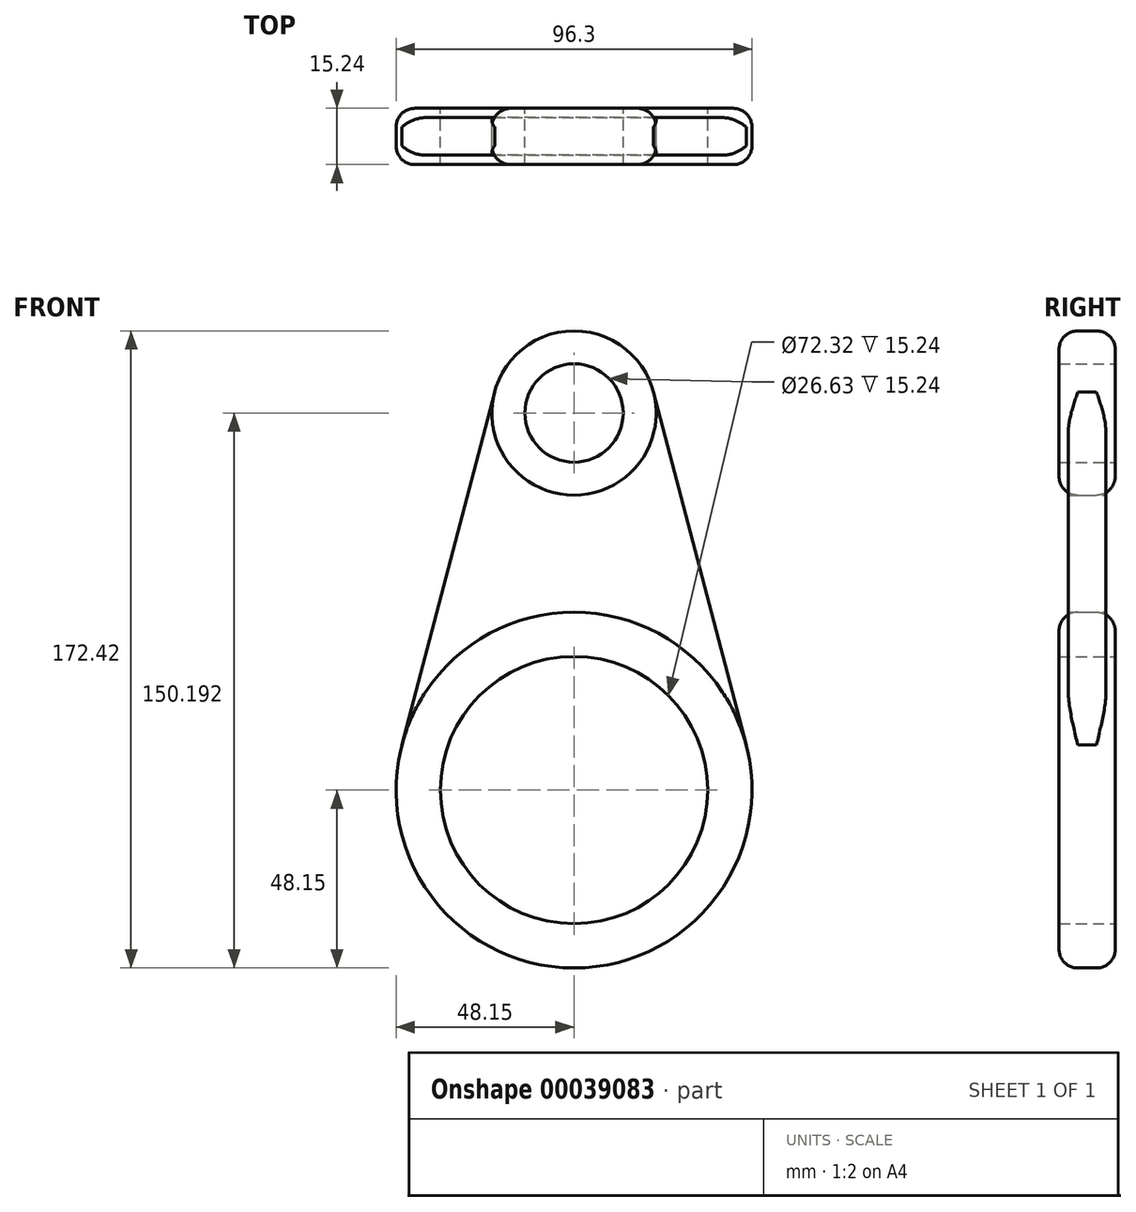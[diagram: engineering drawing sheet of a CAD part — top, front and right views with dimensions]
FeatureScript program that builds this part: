
annotation { "Feature Type Name" : "Feature", "Feature Type Description" : "" }
export const myFeature = defineFeature(function(context is Context, id is Id, definition is map)
    precondition{}
    {
        {
            var Q0;
            Q0=qCreatedBy(makeId("Front.planeOp"),FACE);
            var sketch = newSketch(context, id + "F0", { "sketchPlane" : qUnion([Q0])});
            skCircle(sketch, "E0", {"center": v(0, 0) * mm, "radius": 48.15 * mm});
            skCircle(sketch, "E1", {"center": v(0, 0) * mm, "radius": 36.16 * mm});
            skCircle(sketch, "E2", {"center": v(0, 102.04) * mm, "radius": 22.23 * mm});
            skCircle(sketch, "E3", {"center": v(0, 102.04) * mm, "radius": 13.31 * mm});
            skLineSegment(sketch, "E4", {"start": v(-21.5, 107.69) * mm, "end": v(-46.57, 12.23) * mm});
            skLineSegment(sketch, "E5", {"start": v(21.5, 107.69) * mm, "end": v(46.57, 12.23) * mm});
            skSolve(sketch);
        }
        {
            var Q0;
            Q0=makeQuery(id+"F0.imprint","IMPRINT",FACE,{"disambiguationData":[TD([[makeQuery(id+"F0.imprint","IMPRINT",EDGE,{"derivedFrom":sQuery(id+"F0.wireOp",EDGE,"E1")}),-1.0]])]});
            var Q1;
            Q1=makeQuery(id+"F0.imprint","IMPRINT",FACE,{"disambiguationData":[TD([[makeQuery(id+"F0.imprint","IMPRINT",EDGE,{"derivedFrom":sQuery(id+"F0.wireOp",EDGE,"E3")}),-1.0]])]});
            extrude(context, id + "F1", {"entities" : qUnion([Q0, Q1]), "depth" : 7.62 * mm, "hasSecondDirection" : true, "secondDirectionOppositeDirection" : true, "secondDirectionDepth" : 7.62 * mm});
        }
        {
            var Q0;
            {var subQ1=sQuery(id+"F0.wireOp",EDGE,"E4");Q0=makeQuery(id+"F0.imprint","IMPRINT",FACE,{"disambiguationData":[TD([[makeQuery(id+"F0.imprint","IMPRINT",EDGE,{"derivedFrom":subQ1}),1.0]])]});}
            extrude(context, id + "F2", {"entities" : qUnion([Q0]), "depth" : 5.08 * mm, "hasSecondDirection" : true, "secondDirectionOppositeDirection" : true, "secondDirectionDepth" : 5.08 * mm});
        }
        {
            var Q0;
            Q0=makeQuery(id+"F1.opExtrude","CAP_EDGE",EDGE,{"disambiguationData":[OSD([sQuery(id+"F0.wireOp",EDGE,"E2")])],"isStart":false});
            var Q1;
            Q1=makeQuery(id+"F1.opExtrude","CAP_EDGE",EDGE,{"disambiguationData":[OSD([sQuery(id+"F0.wireOp",EDGE,"E0")])],"isStart":false});
            var Q2;
            Q2=makeQuery(id+"F1.opExtrude","CAP_EDGE",EDGE,{"disambiguationData":[OSD([sQuery(id+"F0.wireOp",EDGE,"E0")])],"isStart":true});
            var Q3;
            Q3=makeQuery(id+"F1.opExtrude","CAP_EDGE",EDGE,{"disambiguationData":[OSD([sQuery(id+"F0.wireOp",EDGE,"E2")])],"isStart":true});
            fillet(context, id + "F3", {"entities" : qUnion([Q0, Q1, Q2, Q3]), "radius" : 5.08 * mm, "tangentPropagation" : true, "allowEdgeOverflow" : false});
        }
        {
            var Q0;
            Q0=makeQuery(id+"F2.opExtrude","CAP_EDGE",EDGE,{"disambiguationData":[OSD([sQuery(id+"F0.wireOp",EDGE,"E5")])],"isStart":true});
            var Q1;
            Q1=makeQuery(id+"F2.opExtrude","CAP_EDGE",EDGE,{"disambiguationData":[OSD([sQuery(id+"F0.wireOp",EDGE,"E5")])],"isStart":false});
            var Q2;
            Q2=makeQuery(id+"F2.opExtrude","CAP_EDGE",EDGE,{"disambiguationData":[OSD([sQuery(id+"F0.wireOp",EDGE,"E4")])],"isStart":true});
            var Q3;
            Q3=makeQuery(id+"F2.opExtrude","CAP_EDGE",EDGE,{"disambiguationData":[OSD([sQuery(id+"F0.wireOp",EDGE,"E4")])],"isStart":false});
            fillet(context, id + "F4", {"entities" : qUnion([Q0, Q1, Q2, Q3]), "radius" : 2.54 * mm, "tangentPropagation" : true, "allowEdgeOverflow" : false});
        }
    });
